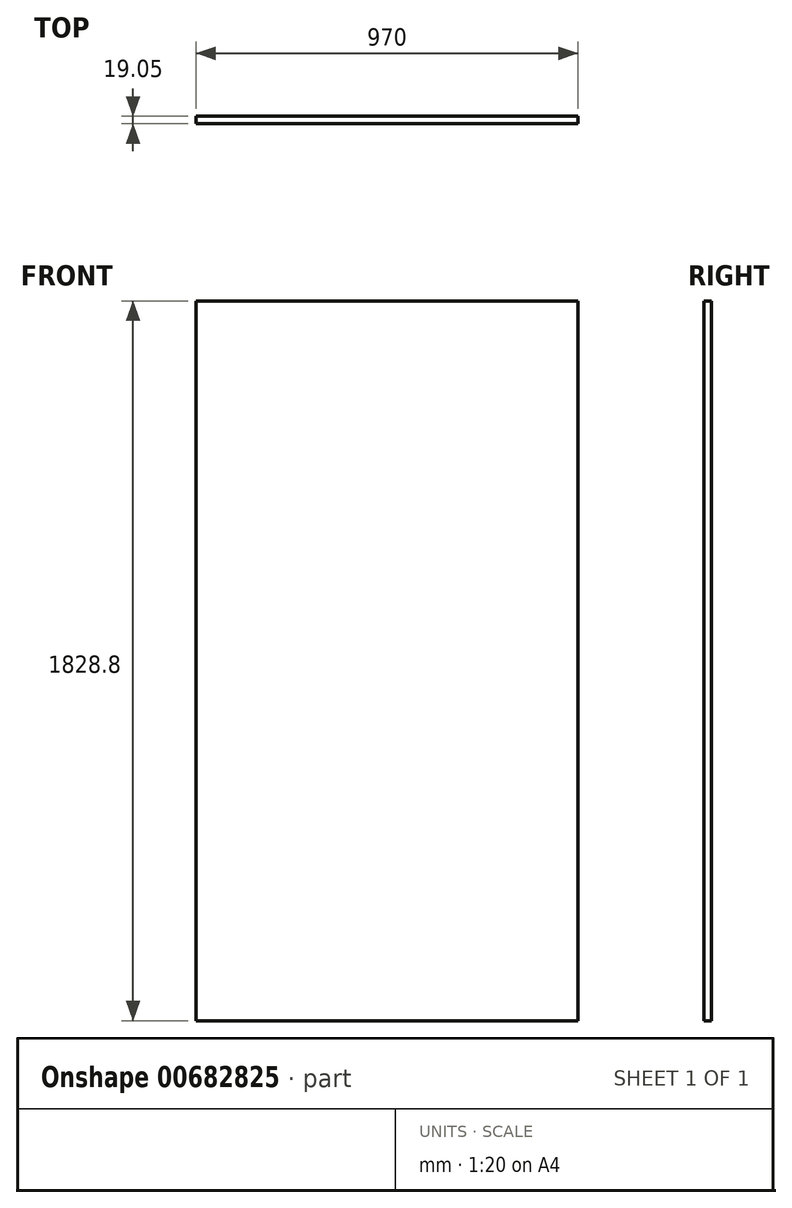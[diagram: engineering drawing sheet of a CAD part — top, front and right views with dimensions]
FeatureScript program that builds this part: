
annotation { "Feature Type Name" : "Feature", "Feature Type Description" : "" }
export const myFeature = defineFeature(function(context is Context, id is Id, definition is map)
    precondition{}
    {
        {
            var Q0;
            Q0=qCreatedBy(makeId("Front.planeOp"),FACE);
            var sketch = newSketch(context, id + "F0", { "sketchPlane" : qUnion([Q0])});
            skLineSegment(sketch, "E0.bottom", {"start": v(0, 0) * mm, "end": v(-970, 0) * mm});
            skLineSegment(sketch, "E0.left", {"start": v(0, 0) * mm, "end": v(0, 1828.8) * mm});
            skLineSegment(sketch, "E0.right", {"start": v(-970, 0) * mm, "end": v(-970, 1828.8) * mm});
            skLineSegment(sketch, "E1", {"start": v(-970, 1117.6) * mm, "end": v(-589, 1117.6) * mm, "construction": true});
            skLineSegment(sketch, "E2", {"start": v(-589, 1117.6) * mm, "end": v(-589, 894.08) * mm, "construction": true});
            skLineSegment(sketch, "E3", {"start": v(-589, 894.08) * mm, "end": v(-392.67, 894.08) * mm, "construction": true});
            skLineSegment(sketch, "E4", {"start": v(-392.67, 894.08) * mm, "end": v(-392.67, 670.56) * mm, "construction": true});
            skLineSegment(sketch, "E5", {"start": v(-392.67, 670.56) * mm, "end": v(-196.33, 670.56) * mm, "construction": true});
            skLineSegment(sketch, "E6", {"start": v(-196.33, 670.56) * mm, "end": v(-196.33, 447.04) * mm, "construction": true});
            skLineSegment(sketch, "E7", {"start": v(-196.33, 447.04) * mm, "end": v(0, 447.04) * mm, "construction": true});
            skLineSegment(sketch, "E8", {"start": v(0, 223.52) * mm, "end": v(196.33, 223.52) * mm, "construction": true});
            skLineSegment(sketch, "E9", {"start": v(196.33, 223.52) * mm, "end": v(196.33, 0) * mm, "construction": true});
            skLineSegment(sketch, "E10", {"start": v(-98.17, 447.04) * mm, "end": v(-98.17, 223.52) * mm, "construction": true});
            skLineSegment(sketch, "E11", {"start": v(-98.17, 223.52) * mm, "end": v(0, 223.52) * mm, "construction": true});
            skLineSegment(sketch, "E12", {"start": v(-589, 1117.6) * mm, "end": v(-392.67, 894.08) * mm, "construction": true});
            skLineSegment(sketch, "E13", {"start": v(0, 1828.8) * mm, "end": v(-970, 1828.8) * mm});
            skSolve(sketch);
        }
        {
            var Q0;
            Q0=qSketchRegion(id+"F0",true);
            extrude(context, id + "F1", {"entities" : qUnion([Q0]), "depth" : 19.05 * mm, "offsetDistance" : 25.4 * mm});
        }
    });
